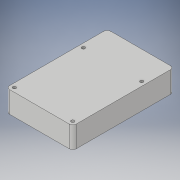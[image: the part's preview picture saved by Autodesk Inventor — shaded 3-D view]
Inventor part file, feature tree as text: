
AUTODESK INVENTOR PART (.ipt)
format: ipt  version: 2017 (Build 210142000, 142)  size: 119,808 bytes
history: native  units: mm
features: extrude x2, sketch x2, fillet x1
ambient origin geometry x8: Origin, YZ Plane, XZ Plane, XY Plane, X Axis, Y Axis, Z Axis, Center Point
bodies: Solid1 (feature_tree)
feature tree (5):
  extrude  "Extrusion1"  Depth=56.0mm
  extrude  "Extrusion2"  Depth=3.0mm
  fillet  "Fillet1"  Radius=3.5mm
  sketch  "Sketch1"  dims[d0=85.0mm d1=56.0mm]
  sketch  "Sketch2"  dims[d2=18.0mm d3=0.0mm d4=3.5mm d5=3.5mm d6=58.0mm d7=2.75mm d8=3.5mm d9=18.0mm d10=0.0mm d11=3.0mm]
